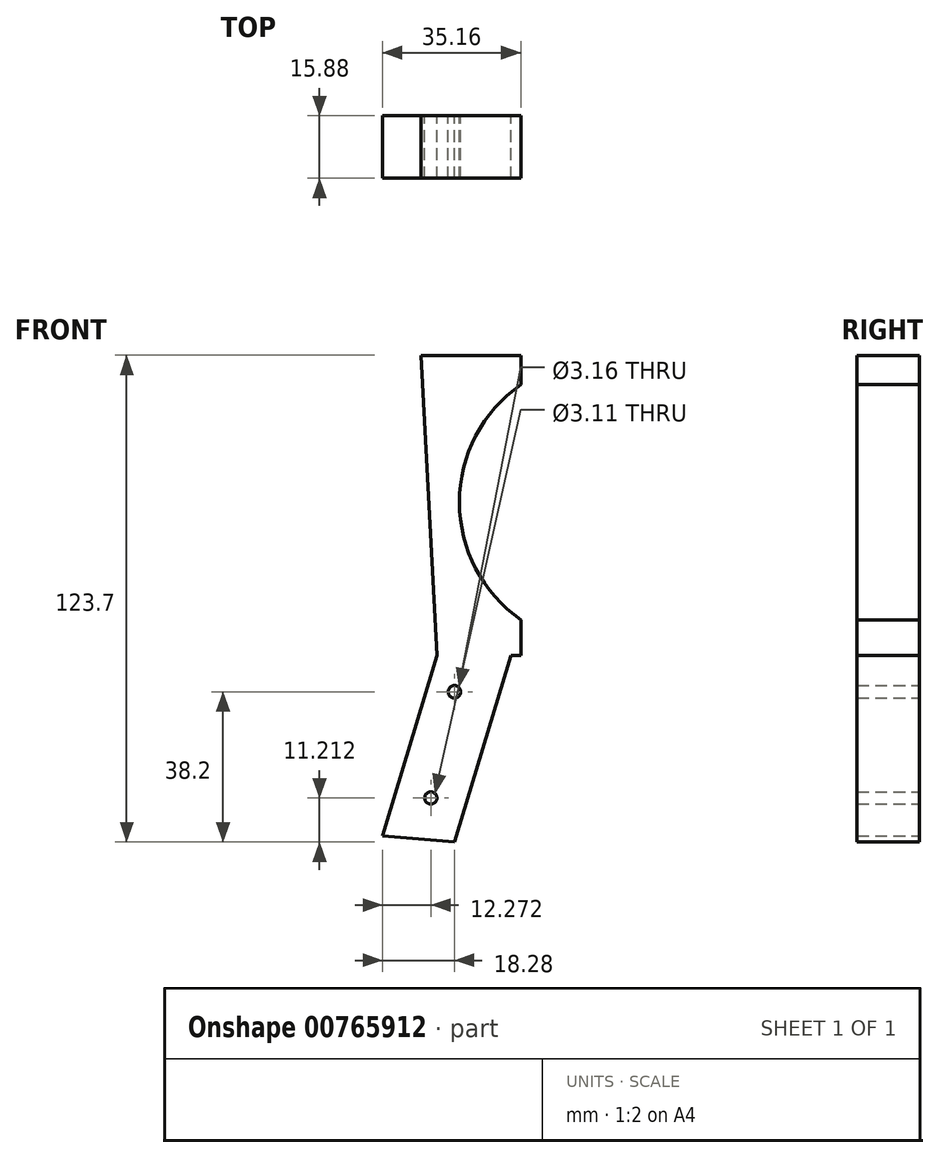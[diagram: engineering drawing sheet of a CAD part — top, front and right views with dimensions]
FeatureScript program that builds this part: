
annotation { "Feature Type Name" : "Feature", "Feature Type Description" : "" }
export const myFeature = defineFeature(function(context is Context, id is Id, definition is map)
    precondition{}
    {
        {
            var Q0;
            Q0=qCreatedBy(makeId("Front.planeOp"),FACE);
            var sketch = newSketch(context, id + "F0", { "sketchPlane" : qUnion([Q0])});
            skLineSegment(sketch, "E0", {"start": v(14.31, -9.01) * mm, "end": v(-4.42, -9.01) * mm});
            skLineSegment(sketch, "E1", {"start": v(14.31, -9.01) * mm, "end": v(16.88, -9.01) * mm});
            skLineSegment(sketch, "E2", {"start": v(16.88, 59.73) * mm, "end": v(16.88, 67.19) * mm});
            skLineSegment(sketch, "E3", {"start": v(16.88, 67.19) * mm, "end": v(-8.52, 67.19) * mm});
            skCircle(sketch, "E4", {"center": v(0, -18.31) * mm, "radius": 1.58 * mm});
            skLineSegment(sketch, "E5", {"start": v(-8.52, 67.19) * mm, "end": v(-4.42, -9.01) * mm});
            skArc(sketch, "E6", {"start": v(16.88, 59.73) * mm, "mid": v(1.27, 29.86) * mm, "end": v(16.88, 0) * mm});
            skLineSegment(sketch, "E7", {"start": v(16.88, 0) * mm, "end": v(16.88, -9.01) * mm});
            skLineSegment(sketch, "E8", {"start": v(14.31, -9.01) * mm, "end": v(0, -56.5) * mm});
            skLineSegment(sketch, "E9", {"start": v(-4.42, -9.01) * mm, "end": v(-18.28, -54.97) * mm});
            skLineSegment(sketch, "E10", {"start": v(-18.28, -54.97) * mm, "end": v(0, -56.5) * mm});
            skCircle(sketch, "E11", {"center": v(-6, -45.3) * mm, "radius": 1.56 * mm});
            skSolve(sketch);
        }
        {
            var Q0;
            Q0=makeQuery(id+"F0.imprint","IMPRINT",FACE,{"disambiguationData":[TD([[makeQuery(id+"F0.imprint","IMPRINT",EDGE,{"derivedFrom":sQuery(id+"F0.wireOp",EDGE,"E0")}),-1.0]])]});
            var Q1;
            Q1=makeQuery(id+"F0.imprint","IMPRINT",FACE,{"disambiguationData":[TD([[makeQuery(id+"F0.imprint","IMPRINT",EDGE,{"derivedFrom":sQuery(id+"F0.wireOp",EDGE,"hOyUH11Z-QOWN-eLGK-8PgL-ONFPwuPvL23o")}),1.0]])]});
            var Q2;
            Q2=makeQuery(id+"F0.imprint","IMPRINT",FACE,{"disambiguationData":[TD([[makeQuery(id+"F0.imprint","IMPRINT",EDGE,{"derivedFrom":sQuery(id+"F0.wireOp",EDGE,"E0")}),1.0]])]});
            extrude(context, id + "F1", {"entities" : qUnion([Q0, Q1, Q2]), "endBound" : BoundingType.SYMMETRIC, "depth" : 15.88 * mm, "offsetDistance" : 25.4 * mm});
        }
    });
